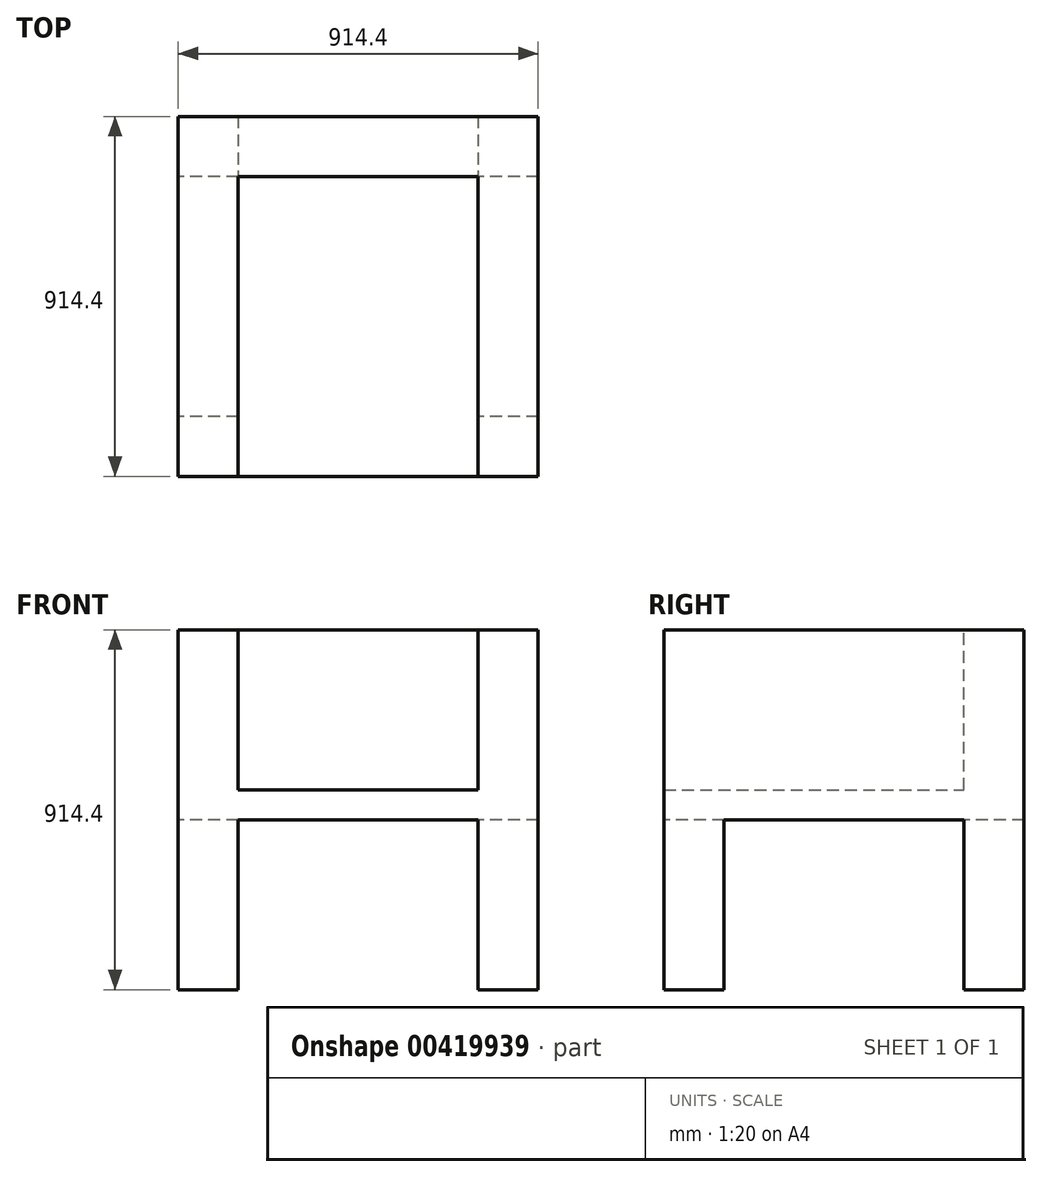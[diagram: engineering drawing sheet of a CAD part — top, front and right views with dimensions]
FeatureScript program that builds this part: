
annotation { "Feature Type Name" : "Feature", "Feature Type Description" : "" }
export const myFeature = defineFeature(function(context is Context, id is Id, definition is map)
    precondition{}
    {
        {
            var Q0;
            Q0=qCreatedBy(makeId("Top.planeOp"),FACE);
            var sketch = newSketch(context, id + "F0", { "sketchPlane" : qUnion([Q0])});
            skLineSegment(sketch, "E0.bottom", {"start": v(-454.63, 501.69) * mm, "end": v(459.77, 501.69) * mm});
            skLineSegment(sketch, "E0.top", {"start": v(-454.63, -412.71) * mm, "end": v(459.77, -412.71) * mm});
            skLineSegment(sketch, "E0.left", {"start": v(-454.63, 501.69) * mm, "end": v(-454.63, -412.71) * mm});
            skLineSegment(sketch, "E0.right", {"start": v(459.77, 501.69) * mm, "end": v(459.77, -412.71) * mm});
            skSolve(sketch);
        }
        {
            var Q0;
            Q0 = qSketchRegion(id + "F0", true);
            extrude(context, id + "F1", {"entities" : qUnion([Q0]), "depth" : 914.4 * mm});
        }
        {
            var Q0;
            Q0=makeQuery(id+"F1.opExtrude","CAP_FACE",FACE,{"disambiguationData":[OSD([sQuery(id+"F0.wireOp",EDGE,"E0.bottom"),sQuery(id+"F0.wireOp",EDGE,"E0.top"),sQuery(id+"F0.wireOp",EDGE,"E0.left"),sQuery(id+"F0.wireOp",EDGE,"E0.right")])],"isStart":false});
            var sketch = newSketch(context, id + "F2", { "sketchPlane" : qUnion([Q0])});
            skLineSegment(sketch, "E1.bottom", {"start": v(307.37, 349.29) * mm, "end": v(-302.23, 349.29) * mm});
            skLineSegment(sketch, "E1.top", {"start": v(307.37, -412.71) * mm, "end": v(-302.23, -412.71) * mm});
            skLineSegment(sketch, "E1.left", {"start": v(307.37, -412.71) * mm, "end": v(307.37, 349.29) * mm});
            skLineSegment(sketch, "E1.right", {"start": v(-302.23, 349.29) * mm, "end": v(-302.23, -412.71) * mm});
            skSolve(sketch);
        }
        {
            var Q0;
            Q0 = qSketchRegion(id + "F2", true);
            extrude(context, id + "F3", {"entities" : qUnion([Q0]), "operationType" : NewBodyOperationType.REMOVE, "oppositeDirection" : true, "depth" : 406.4 * mm});
        }
        {
            var Q0;
            Q0=makeQuery(id+"F1.opExtrude","SWEPT_FACE",FACE,{"disambiguationData":[OSD([sQuery(id+"F0.wireOp",EDGE,"E0.top")])]});
            var sketch = newSketch(context, id + "F4", { "sketchPlane" : qUnion([Q0])});
            skLineSegment(sketch, "E2.bottom", {"start": v(-302.23, 431.8) * mm, "end": v(307.37, 431.8) * mm});
            skLineSegment(sketch, "E2.top", {"start": v(-302.23, 0) * mm, "end": v(307.37, 0) * mm});
            skLineSegment(sketch, "E2.left", {"start": v(-302.23, 431.8) * mm, "end": v(-302.23, 0) * mm});
            skLineSegment(sketch, "E2.right", {"start": v(307.37, 431.8) * mm, "end": v(307.37, 0) * mm});
            skSolve(sketch);
        }
        {
            var Q0;
            Q0 = qSketchRegion(id + "F4", true);
            extrude(context, id + "F5", {"entities" : qUnion([Q0]), "operationType" : NewBodyOperationType.REMOVE, "endBound" : BoundingType.THROUGH_ALL, "oppositeDirection" : true, "depth" : 25.4 * mm});
        }
        {
            var Q0;
            Q0=makeQuery(id+"F1.opExtrude","SWEPT_FACE",FACE,{"disambiguationData":[OSD([sQuery(id+"F0.wireOp",EDGE,"E0.left")])]});
            var sketch = newSketch(context, id + "F6", { "sketchPlane" : qUnion([Q0])});
            skLineSegment(sketch, "E3.bottom", {"start": v(-349.29, 431.8) * mm, "end": v(260.31, 431.8) * mm});
            skLineSegment(sketch, "E3.top", {"start": v(-349.29, 0) * mm, "end": v(260.31, 0) * mm});
            skLineSegment(sketch, "E3.left", {"start": v(-349.29, 431.8) * mm, "end": v(-349.29, 0) * mm});
            skLineSegment(sketch, "E3.right", {"start": v(260.31, 431.8) * mm, "end": v(260.31, 0) * mm});
            skSolve(sketch);
        }
        {
            var Q0;
            Q0 = qSketchRegion(id + "F6", true);
            extrude(context, id + "F7", {"entities" : qUnion([Q0]), "operationType" : NewBodyOperationType.REMOVE, "endBound" : BoundingType.THROUGH_ALL, "oppositeDirection" : true, "depth" : 25.4 * mm});
        }
    });
